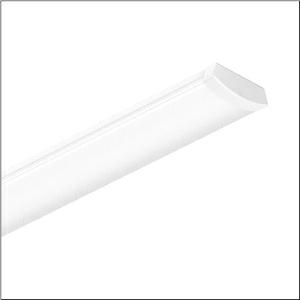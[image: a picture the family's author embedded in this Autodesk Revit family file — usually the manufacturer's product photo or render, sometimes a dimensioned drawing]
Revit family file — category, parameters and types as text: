
# Revit family: siluette_21_51ln12mnm70a3g
name_source: partatom
category: Lighting Fixtures
units: mm (PartAtom-declared; Revit-internal decimal feet)

## family parameters
Cut with Voids When Loaded = No
Host = Face
Light Source = No
Part Type = Normal
Room Calculation Point = No
Round Connector Dimension = Use Diameter
Shared = No

## types (1)
- --- (1 x LED, 4320 lm, 28.8 W, 5000K)
    Apparent Load = 29 VA
    CIE Flux Codes = 43 73 92 94 100
    Color Rendering = 80
    Color Temperature = 5000K
    Default Elevation = 1800 mm
    Description = Siluette 21, office luminaire, primary optical cover: enclosure, of PC, frosted, light emission: direct distribution, primary light characteristic: symmetric, installation type: suspended mounting, surface-mounted, LED, rated luminous flux: 7.150lm, luminous efficacy: 142lm/W, light colour: 830/840/850, colour temperature: 3000/4000/5000K, control gear: ON/OFF Multilumen, with terminal, 4-pole, mains connection: 220..240V, AC, 50/60Hz, rated input power: 51W, control gear: single battery element, housing, of sheet steel, white, length: 1.500mm, width: 152mm, height: 53mm, end cap, of PMMA, white, protection rating (complete): IP44, insulation class (complete): insulation class I (protective earthing), certification: CE, UKCA, protection symbol: D, impact resistance: IK04, permissible operating ambient temperature: +5..+40°C, standard: EN 60598-2-22, corresponds to IFS (International Featured Standards) requirements for safety and quality in the food industry, contact your sales advisor before using the luminaires in applications with unclear chemical exposure, large temperature fluctuations or condensation-forming humidity, packaging unit: 1 piece
    Height = 52 mm  [stored 0.170604 ft]
    Lamp = 1 x LED
    Lamp Light Flux = 4320 lm
    Lamp Power = 28.8 W
    Lamp count = 1
    Length = 1485 mm
    Luminous efficacy = 150 lm/W
    Manufacturer = Siteco
    ModVariant = No
    Model = 51LN12MNM70A3G
    Mounting Place = Ceiling
    Mounting Type = Pendant
    Number of Poles = 1
    OnlyDefault = Yes
    Power Factor = 1
    Product Name = Siluette 21
    Product group = office luminaire | ceiling pendant
    ProductGroupID = 903
    Protection Class = Protection class I
    Protection Degree = IP 44
    RLX_Detail_Level = 1
    RLX_Emergency_Light_Flux = 0 lm
    RLX_Emergency_Type = 0
    RLX_Emergency_Type_DB = No
    RlxData = <blob elided: 19505 chars, md5=d0f5361c>
    Socket = socket
    Standby Power = 0 W
    System Light Flux = 4320 lm
    System Power = 29 W
    Type Comments = individual setting: colour temperature 5000K, luminous flux: 61 % | (OFF | OFF | ON) | 200 mA
    Type Image = l_1296910.jpg
    URL = http://relux.com
    VarID = @adj_067333
    Voltage = 0 V
    Weight = 0.00 kg
    Width = 152 mm

note: [stored X ft] marks values corroborated as IEEE doubles in the binary element streams (Revit-internal decimal feet)

## geometry (parser evidence)
native form markers: Blend x4, Sweep x11
no freeform markers — native parametric forms only
